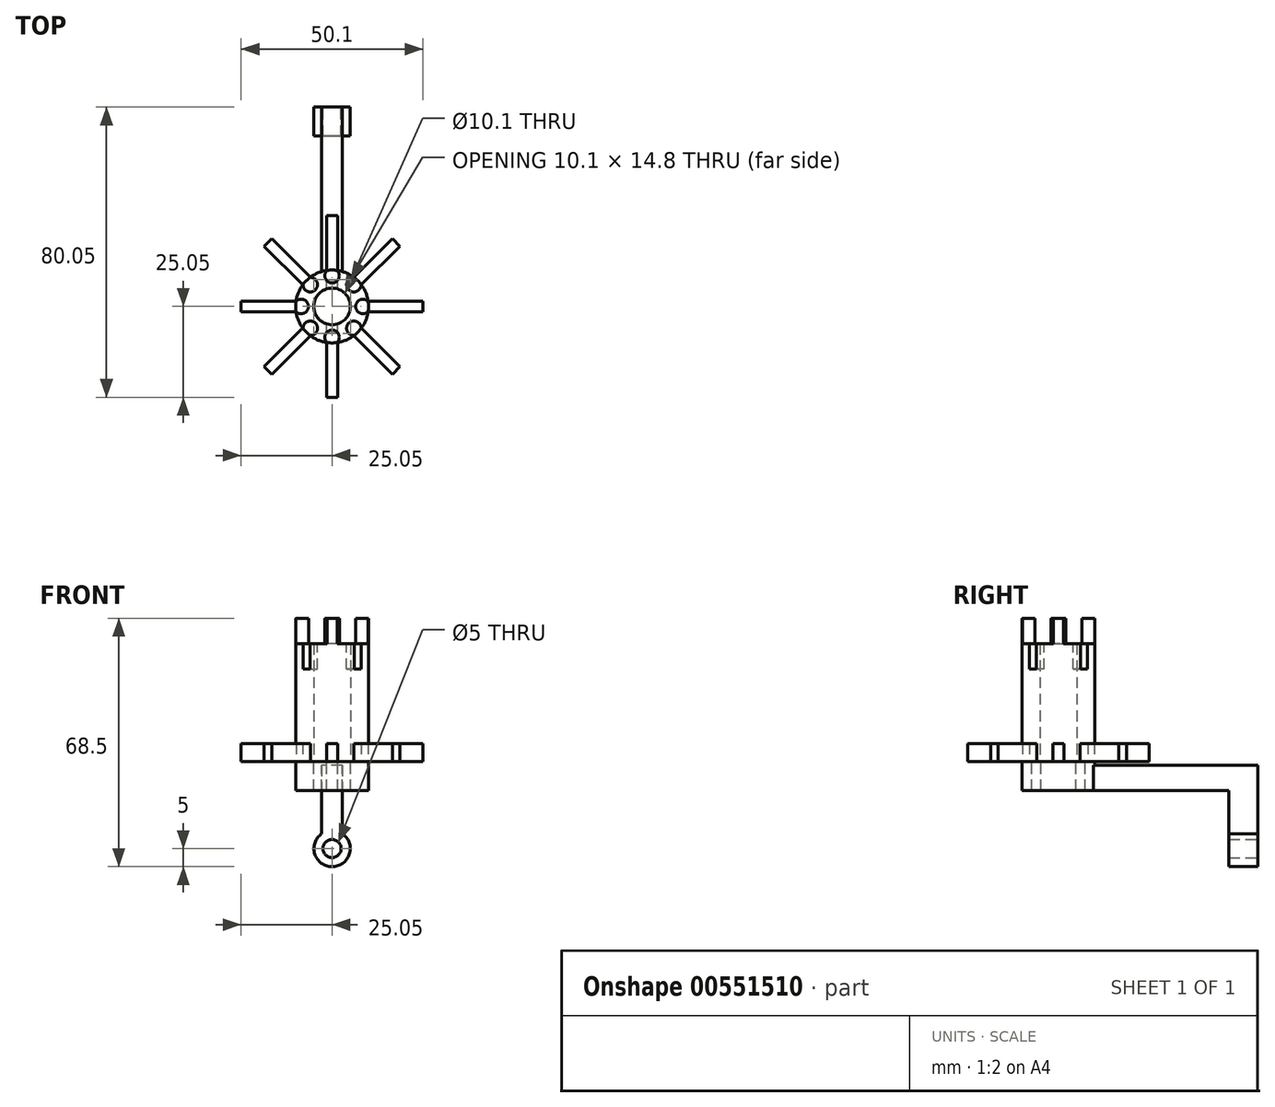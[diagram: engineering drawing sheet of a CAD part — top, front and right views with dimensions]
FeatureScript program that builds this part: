
annotation { "Feature Type Name" : "Feature", "Feature Type Description" : "" }
export const myFeature = defineFeature(function(context is Context, id is Id, definition is map)
    precondition{}
    {
        {
            var Q0;
            Q0=qCreatedBy(makeId("Front.planeOp"),FACE);
            var sketch = newSketch(context, id + "F0", { "sketchPlane" : qUnion([Q0])});
            skLineSegment(sketch, "E0.bottom", {"start": v(2.83, -1) * mm, "end": v(-2.83, -1) * mm});
            skLineSegment(sketch, "E0.top", {"start": v(2.83, -8) * mm, "end": v(-2.83, -8) * mm});
            skLineSegment(sketch, "E0.left", {"start": v(2.83, -1) * mm, "end": v(2.83, -8) * mm});
            skLineSegment(sketch, "E0.right", {"start": v(-2.83, -1) * mm, "end": v(-2.83, -8) * mm});
            skSolve(sketch);
        }
        {
            var Q0;
            Q0=qCreatedBy(makeId("Top.planeOp"),FACE);
            var sketch = newSketch(context, id + "F1", { "sketchPlane" : qUnion([Q0])});
            skCircle(sketch, "E1", {"center": v(0, 0) * mm, "radius": 5.05 * mm});
            skCircle(sketch, "E2", {"center": v(0, 0) * mm, "radius": 10.05 * mm});
            skLineSegment(sketch, "E3.bottom", {"start": v(1.5, -25.05) * mm, "end": v(-1.5, -25.05) * mm});
            skLineSegment(sketch, "E3.top", {"start": v(1.5, 25.05) * mm, "end": v(-1.5, 25.05) * mm});
            skLineSegment(sketch, "E3.left", {"start": v(1.5, -25.05) * mm, "end": v(1.5, 25.05) * mm});
            skLineSegment(sketch, "E3.right", {"start": v(-1.5, -25.05) * mm, "end": v(-1.5, 25.05) * mm});
            skLineSegment(sketch, "E4.bottom", {"start": v(25.05, -1.5) * mm, "end": v(-25.05, -1.5) * mm});
            skLineSegment(sketch, "E4.top", {"start": v(25.05, 1.5) * mm, "end": v(-25.05, 1.5) * mm});
            skLineSegment(sketch, "E4.left", {"start": v(25.05, -1.5) * mm, "end": v(25.05, 1.5) * mm});
            skLineSegment(sketch, "E4.right", {"start": v(-25.05, -1.5) * mm, "end": v(-25.05, 1.5) * mm});
            skLineSegment(sketch, "E5", {"start": v(18.74, -16.62) * mm, "end": v(-16.62, 18.74) * mm});
            skLineSegment(sketch, "E6", {"start": v(16.62, -18.74) * mm, "end": v(-18.74, 16.62) * mm});
            skLineSegment(sketch, "E7", {"start": v(-18.74, 16.62) * mm, "end": v(-16.62, 18.74) * mm});
            skLineSegment(sketch, "E8", {"start": v(16.62, -18.74) * mm, "end": v(18.74, -16.62) * mm});
            skLineSegment(sketch, "E9", {"start": v(-18.74, -16.62) * mm, "end": v(16.62, 18.74) * mm});
            skLineSegment(sketch, "E10", {"start": v(18.74, 16.62) * mm, "end": v(-16.62, -18.74) * mm});
            skLineSegment(sketch, "E11", {"start": v(-18.74, -16.62) * mm, "end": v(-16.62, -18.74) * mm});
            skLineSegment(sketch, "E12", {"start": v(16.62, 18.74) * mm, "end": v(18.74, 16.62) * mm});
            skLineSegment(sketch, "E13", {"start": v(1.5, -7.4) * mm, "end": v(-1.5, -7.4) * mm});
            skLineSegment(sketch, "E14", {"start": v(-1.5, 7.4) * mm, "end": v(1.5, 7.4) * mm});
            skSolve(sketch);
        }
        {
            var Q0;
            {var subQ0=sQuery(id+"F1.wireOp",EDGE,"E5");var subQ1=sQuery(id+"F1.wireOp",EDGE,"E1");var subQ2=makeQuery(id+"F1.imprint","INTERSECT",VERTEX,{"disambiguationData":[OD(1.0)],"derivedFrom":[subQ1,subQ0]});Q0=makeQuery(id+"F1.imprint","IMPRINT",FACE,{"disambiguationData":[TD([[makeQuery(id+"F1.imprint","IMPRINT",EDGE,{"disambiguationData":[TD([[subQ2,-1.0]])],"derivedFrom":subQ1}),-1.0]])]});}
            var Q1;
            {var subQ0=sQuery(id+"F1.wireOp",EDGE,"E6");var subQ1=sQuery(id+"F1.wireOp",EDGE,"E1");var subQ2=makeQuery(id+"F1.imprint","INTERSECT",VERTEX,{"disambiguationData":[OD(1.0)],"derivedFrom":[subQ1,subQ0]});Q1=makeQuery(id+"F1.imprint","IMPRINT",FACE,{"disambiguationData":[TD([[makeQuery(id+"F1.imprint","IMPRINT",EDGE,{"disambiguationData":[TD([[subQ2,-1.0]])],"derivedFrom":subQ1}),-1.0]])]});}
            var Q2;
            {var subQ0=sQuery(id+"F1.wireOp",EDGE,"E3.left");var subQ1=sQuery(id+"F1.wireOp",EDGE,"E1");var subQ2=makeQuery(id+"F1.imprint","INTERSECT",VERTEX,{"disambiguationData":[OD(1.0)],"derivedFrom":[subQ1,subQ0]});Q2=makeQuery(id+"F1.imprint","IMPRINT",FACE,{"disambiguationData":[TD([[makeQuery(id+"F1.imprint","IMPRINT",EDGE,{"disambiguationData":[TD([[subQ2,-1.0]])],"derivedFrom":subQ1}),-1.0]])]});}
            var Q3;
            {var subQ0=sQuery(id+"F1.wireOp",EDGE,"E3.right");var subQ1=sQuery(id+"F1.wireOp",EDGE,"E1");var subQ2=makeQuery(id+"F1.imprint","INTERSECT",VERTEX,{"disambiguationData":[OD(1.0)],"derivedFrom":[subQ1,subQ0]});Q3=makeQuery(id+"F1.imprint","IMPRINT",FACE,{"disambiguationData":[TD([[makeQuery(id+"F1.imprint","IMPRINT",EDGE,{"disambiguationData":[TD([[subQ2,-1.0]])],"derivedFrom":subQ1}),-1.0]])]});}
            var Q4;
            {var subQ0=sQuery(id+"F1.wireOp",EDGE,"E10");var subQ1=sQuery(id+"F1.wireOp",EDGE,"E1");var subQ2=makeQuery(id+"F1.imprint","INTERSECT",VERTEX,{"disambiguationData":[OD(1.0)],"derivedFrom":[subQ1,subQ0]});Q4=makeQuery(id+"F1.imprint","IMPRINT",FACE,{"disambiguationData":[TD([[makeQuery(id+"F1.imprint","IMPRINT",EDGE,{"disambiguationData":[TD([[subQ2,-1.0]])],"derivedFrom":subQ1}),-1.0]])]});}
            var Q5;
            {var subQ0=sQuery(id+"F1.wireOp",EDGE,"E9");var subQ1=sQuery(id+"F1.wireOp",EDGE,"E1");var subQ2=makeQuery(id+"F1.imprint","INTERSECT",VERTEX,{"disambiguationData":[OD(1.0)],"derivedFrom":[subQ1,subQ0]});Q5=makeQuery(id+"F1.imprint","IMPRINT",FACE,{"disambiguationData":[TD([[makeQuery(id+"F1.imprint","IMPRINT",EDGE,{"disambiguationData":[TD([[subQ2,-1.0]])],"derivedFrom":subQ1}),-1.0]])]});}
            var Q6;
            {var subQ0=sQuery(id+"F1.wireOp",EDGE,"E4.bottom");var subQ1=sQuery(id+"F1.wireOp",EDGE,"E1");var subQ2=makeQuery(id+"F1.imprint","INTERSECT",VERTEX,{"disambiguationData":[OD(0.0)],"derivedFrom":[subQ1,subQ0]});Q6=makeQuery(id+"F1.imprint","IMPRINT",FACE,{"disambiguationData":[TD([[makeQuery(id+"F1.imprint","IMPRINT",EDGE,{"disambiguationData":[TD([[subQ2,-1.0]])],"derivedFrom":subQ1}),-1.0]])]});}
            var Q7;
            {var subQ0=sQuery(id+"F1.wireOp",EDGE,"E4.top");var subQ1=sQuery(id+"F1.wireOp",EDGE,"E1");var subQ2=makeQuery(id+"F1.imprint","INTERSECT",VERTEX,{"disambiguationData":[OD(1.0)],"derivedFrom":[subQ1,subQ0]});Q7=makeQuery(id+"F1.imprint","IMPRINT",FACE,{"disambiguationData":[TD([[makeQuery(id+"F1.imprint","IMPRINT",EDGE,{"disambiguationData":[TD([[subQ2,-1.0]])],"derivedFrom":subQ1}),-1.0]])]});}
            var Q8;
            {var subQ0=sQuery(id+"F1.wireOp",EDGE,"E6");var subQ1=sQuery(id+"F1.wireOp",EDGE,"E1");var subQ2=makeQuery(id+"F1.imprint","INTERSECT",VERTEX,{"disambiguationData":[OD(0.0)],"derivedFrom":[subQ1,subQ0]});Q8=makeQuery(id+"F1.imprint","IMPRINT",FACE,{"disambiguationData":[TD([[makeQuery(id+"F1.imprint","IMPRINT",EDGE,{"disambiguationData":[TD([[subQ2,-1.0]])],"derivedFrom":subQ1}),-1.0]])]});}
            var Q9;
            {var subQ0=sQuery(id+"F1.wireOp",EDGE,"E5");var subQ1=sQuery(id+"F1.wireOp",EDGE,"E1");var subQ2=makeQuery(id+"F1.imprint","INTERSECT",VERTEX,{"disambiguationData":[OD(0.0)],"derivedFrom":[subQ1,subQ0]});Q9=makeQuery(id+"F1.imprint","IMPRINT",FACE,{"disambiguationData":[TD([[makeQuery(id+"F1.imprint","IMPRINT",EDGE,{"disambiguationData":[TD([[subQ2,-1.0]])],"derivedFrom":subQ1}),-1.0]])]});}
            var Q10;
            {var subQ0=sQuery(id+"F1.wireOp",EDGE,"E3.right");var subQ1=sQuery(id+"F1.wireOp",EDGE,"E1");var subQ2=makeQuery(id+"F1.imprint","INTERSECT",VERTEX,{"disambiguationData":[OD(0.0)],"derivedFrom":[subQ1,subQ0]});Q10=makeQuery(id+"F1.imprint","IMPRINT",FACE,{"disambiguationData":[TD([[makeQuery(id+"F1.imprint","IMPRINT",EDGE,{"disambiguationData":[TD([[subQ2,-1.0]])],"derivedFrom":subQ1}),-1.0]])]});}
            var Q11;
            {var subQ0=sQuery(id+"F1.wireOp",EDGE,"E3.left");var subQ1=sQuery(id+"F1.wireOp",EDGE,"E1");var subQ2=makeQuery(id+"F1.imprint","INTERSECT",VERTEX,{"disambiguationData":[OD(0.0)],"derivedFrom":[subQ1,subQ0]});Q11=makeQuery(id+"F1.imprint","IMPRINT",FACE,{"disambiguationData":[TD([[makeQuery(id+"F1.imprint","IMPRINT",EDGE,{"disambiguationData":[TD([[subQ2,-1.0]])],"derivedFrom":subQ1}),-1.0]])]});}
            var Q12;
            {var subQ0=sQuery(id+"F1.wireOp",EDGE,"E9");var subQ1=sQuery(id+"F1.wireOp",EDGE,"E1");var subQ2=makeQuery(id+"F1.imprint","INTERSECT",VERTEX,{"disambiguationData":[OD(0.0)],"derivedFrom":[subQ1,subQ0]});Q12=makeQuery(id+"F1.imprint","IMPRINT",FACE,{"disambiguationData":[TD([[makeQuery(id+"F1.imprint","IMPRINT",EDGE,{"disambiguationData":[TD([[subQ2,-1.0]])],"derivedFrom":subQ1}),-1.0]])]});}
            var Q13;
            {var subQ0=sQuery(id+"F1.wireOp",EDGE,"E10");var subQ1=sQuery(id+"F1.wireOp",EDGE,"E1");var subQ2=makeQuery(id+"F1.imprint","INTERSECT",VERTEX,{"disambiguationData":[OD(0.0)],"derivedFrom":[subQ1,subQ0]});Q13=makeQuery(id+"F1.imprint","IMPRINT",FACE,{"disambiguationData":[TD([[makeQuery(id+"F1.imprint","IMPRINT",EDGE,{"disambiguationData":[TD([[subQ2,-1.0]])],"derivedFrom":subQ1}),-1.0]])]});}
            var Q14;
            {var subQ0=sQuery(id+"F1.wireOp",EDGE,"E10");var subQ1=sQuery(id+"F1.wireOp",EDGE,"E1");var subQ2=makeQuery(id+"F1.imprint","INTERSECT",VERTEX,{"disambiguationData":[OD(0.0)],"derivedFrom":[subQ1,subQ0]});Q14=makeQuery(id+"F1.imprint","IMPRINT",FACE,{"disambiguationData":[TD([[makeQuery(id+"F1.imprint","IMPRINT",EDGE,{"disambiguationData":[TD([[subQ2,1.0]])],"derivedFrom":subQ1}),-1.0]])]});}
            var Q15;
            {var subQ0=sQuery(id+"F1.wireOp",EDGE,"E4.top");var subQ1=sQuery(id+"F1.wireOp",EDGE,"E1");var subQ2=makeQuery(id+"F1.imprint","INTERSECT",VERTEX,{"disambiguationData":[OD(0.0)],"derivedFrom":[subQ1,subQ0]});Q15=makeQuery(id+"F1.imprint","IMPRINT",FACE,{"disambiguationData":[TD([[makeQuery(id+"F1.imprint","IMPRINT",EDGE,{"disambiguationData":[TD([[subQ2,1.0]])],"derivedFrom":subQ1}),-1.0]])]});}
            var Q16;
            {var subQ5=sQuery(id+"F1.wireOp",EDGE,"E13");Q16=makeQuery(id+"F1.imprint","IMPRINT",FACE,{"disambiguationData":[TD([[makeQuery(id+"F1.imprint","IMPRINT",EDGE,{"derivedFrom":subQ5}),1.0]])]});}
            var Q17;
            {var subQ5=sQuery(id+"F1.wireOp",EDGE,"E14");Q17=makeQuery(id+"F1.imprint","IMPRINT",FACE,{"disambiguationData":[TD([[makeQuery(id+"F1.imprint","IMPRINT",EDGE,{"derivedFrom":subQ5}),1.0]])]});}
            extrude(context, id + "F2", {"entities" : qUnion([Q0, Q1, Q2, Q3, Q4, Q5, Q6, Q7, Q8, Q9, Q10, Q11, Q12, Q13, Q14, Q15, Q16, Q17]), "depth" : 32.5 * mm, "offsetDistance" : 25 * mm});
        }
        {
            var Q0;
            {var subQ5=sQuery(id+"F1.wireOp",EDGE,"E4.right");Q0=makeQuery(id+"F1.imprint","IMPRINT",FACE,{"disambiguationData":[TD([[makeQuery(id+"F1.imprint","IMPRINT",EDGE,{"derivedFrom":subQ5}),-1.0]])]});}
            var Q1;
            {var subQ5=sQuery(id+"F1.wireOp",EDGE,"E11");Q1=makeQuery(id+"F1.imprint","IMPRINT",FACE,{"disambiguationData":[TD([[makeQuery(id+"F1.imprint","IMPRINT",EDGE,{"derivedFrom":subQ5}),1.0]])]});}
            var Q2;
            {var subQ5=sQuery(id+"F1.wireOp",EDGE,"E3.bottom");Q2=makeQuery(id+"F1.imprint","IMPRINT",FACE,{"disambiguationData":[TD([[makeQuery(id+"F1.imprint","IMPRINT",EDGE,{"derivedFrom":subQ5}),-1.0]])]});}
            var Q3;
            {var subQ5=sQuery(id+"F1.wireOp",EDGE,"E8");Q3=makeQuery(id+"F1.imprint","IMPRINT",FACE,{"disambiguationData":[TD([[makeQuery(id+"F1.imprint","IMPRINT",EDGE,{"derivedFrom":subQ5}),1.0]])]});}
            var Q4;
            {var subQ5=sQuery(id+"F1.wireOp",EDGE,"E4.left");Q4=makeQuery(id+"F1.imprint","IMPRINT",FACE,{"disambiguationData":[TD([[makeQuery(id+"F1.imprint","IMPRINT",EDGE,{"derivedFrom":subQ5}),1.0]])]});}
            var Q5;
            {var subQ5=sQuery(id+"F1.wireOp",EDGE,"E12");Q5=makeQuery(id+"F1.imprint","IMPRINT",FACE,{"disambiguationData":[TD([[makeQuery(id+"F1.imprint","IMPRINT",EDGE,{"derivedFrom":subQ5}),-1.0]])]});}
            var Q6;
            {var subQ5=sQuery(id+"F1.wireOp",EDGE,"E3.top");Q6=makeQuery(id+"F1.imprint","IMPRINT",FACE,{"disambiguationData":[TD([[makeQuery(id+"F1.imprint","IMPRINT",EDGE,{"derivedFrom":subQ5}),1.0]])]});}
            var Q7;
            {var subQ5=sQuery(id+"F1.wireOp",EDGE,"E7");Q7=makeQuery(id+"F1.imprint","IMPRINT",FACE,{"disambiguationData":[TD([[makeQuery(id+"F1.imprint","IMPRINT",EDGE,{"derivedFrom":subQ5}),-1.0]])]});}
            extrude(context, id + "F3", {"entities" : qUnion([Q0, Q1, Q2, Q3, Q4, Q5, Q6, Q7]), "operationType" : NewBodyOperationType.ADD, "depth" : 5 * mm, "offsetDistance" : 25 * mm});
        }
        {
            var Q0;
            Q0=makeQuery(id+"F2.opExtrude","CAP_FACE",FACE,{"disambiguationData":[OSD([sQuery(id+"F1.wireOp",EDGE,"E1"),sQuery(id+"F1.wireOp",EDGE,"E2")])],"isStart":false});
            var sketch = newSketch(context, id + "F4", { "sketchPlane" : qUnion([Q0])});
            skLineSegment(sketch, "E15", {"start": v(0, 0) * mm, "end": v(8.5, 0) * mm});
            skLineSegment(sketch, "E16", {"start": v(0, 0) * mm, "end": v(0, -8.5) * mm});
            skLineSegment(sketch, "E17", {"start": v(0, 0) * mm, "end": v(-8.5, 0) * mm});
            skLineSegment(sketch, "E18", {"start": v(0, 0) * mm, "end": v(0, 8.5) * mm});
            skLineSegment(sketch, "E19", {"start": v(0, 0) * mm, "end": v(6.01, 6.01) * mm});
            skLineSegment(sketch, "E20", {"start": v(0, 0) * mm, "end": v(-6.01, 6.01) * mm});
            skLineSegment(sketch, "E21", {"start": v(0, 0) * mm, "end": v(6.01, -6.01) * mm});
            skLineSegment(sketch, "E22", {"start": v(0, 0) * mm, "end": v(-6.01, -6.01) * mm});
            skCircle(sketch, "E23", {"center": v(-8.5, 0) * mm, "radius": 2 * mm});
            skCircle(sketch, "E24", {"center": v(-6.01, -6.01) * mm, "radius": 2 * mm});
            skCircle(sketch, "E25", {"center": v(0, -8.5) * mm, "radius": 2 * mm});
            skCircle(sketch, "E26", {"center": v(6.01, -6.01) * mm, "radius": 2 * mm});
            skCircle(sketch, "E27", {"center": v(8.5, 0) * mm, "radius": 2 * mm});
            skCircle(sketch, "E28", {"center": v(6.01, 6.01) * mm, "radius": 2 * mm});
            skCircle(sketch, "E29", {"center": v(0, 8.5) * mm, "radius": 2 * mm});
            skCircle(sketch, "E30", {"center": v(-6.01, 6.01) * mm, "radius": 2 * mm});
            skSolve(sketch);
        }
        {
            var Q0;
            Q0=makeQuery(id+"F4.imprint","IMPRINT",FACE,{"disambiguationData":[TD([[makeQuery(id+"F4.imprint","IMPRINT",EDGE,{"derivedFrom":sQuery(id+"F4.wireOp",EDGE,"E25")}),1.0]])]});
            var Q1;
            Q1=makeQuery(id+"F4.imprint","IMPRINT",FACE,{"disambiguationData":[TD([[makeQuery(id+"F4.imprint","IMPRINT",EDGE,{"derivedFrom":sQuery(id+"F4.wireOp",EDGE,"E29")}),1.0]])]});
            var Q2;
            Q2=makeQuery(id+"F4.imprint","IMPRINT",FACE,{"disambiguationData":[TD([[makeQuery(id+"F4.imprint","IMPRINT",EDGE,{"derivedFrom":sQuery(id+"F4.wireOp",EDGE,"E23")}),1.0]])]});
            var Q3;
            Q3=makeQuery(id+"F4.imprint","IMPRINT",FACE,{"disambiguationData":[TD([[makeQuery(id+"F4.imprint","IMPRINT",EDGE,{"derivedFrom":sQuery(id+"F4.wireOp",EDGE,"E27")}),1.0]])]});
            extrude(context, id + "F5", {"entities" : qUnion([Q0, Q1, Q2, Q3]), "operationType" : NewBodyOperationType.ADD, "depth" : 7 * mm, "offsetDistance" : 25 * mm});
        }
        {
            var Q0;
            Q0=makeQuery(id+"F4.imprint","IMPRINT",FACE,{"disambiguationData":[TD([[makeQuery(id+"F4.imprint","IMPRINT",EDGE,{"derivedFrom":sQuery(id+"F4.wireOp",EDGE,"E24")}),1.0]])]});
            var Q1;
            Q1=makeQuery(id+"F4.imprint","IMPRINT",FACE,{"disambiguationData":[TD([[makeQuery(id+"F4.imprint","IMPRINT",EDGE,{"derivedFrom":sQuery(id+"F4.wireOp",EDGE,"E26")}),1.0]])]});
            var Q2;
            Q2=makeQuery(id+"F4.imprint","IMPRINT",FACE,{"disambiguationData":[TD([[makeQuery(id+"F4.imprint","IMPRINT",EDGE,{"derivedFrom":sQuery(id+"F4.wireOp",EDGE,"E28")}),1.0]])]});
            var Q3;
            Q3=makeQuery(id+"F4.imprint","IMPRINT",FACE,{"disambiguationData":[TD([[makeQuery(id+"F4.imprint","IMPRINT",EDGE,{"derivedFrom":sQuery(id+"F4.wireOp",EDGE,"E30")}),1.0]])]});
            extrude(context, id + "F6", {"entities" : qUnion([Q0, Q1, Q2, Q3]), "operationType" : NewBodyOperationType.REMOVE, "oppositeDirection" : true, "depth" : 7 * mm, "offsetDistance" : 25 * mm});
        }
        {
            var Q0;
            {var subQ0=sQuery(id+"F1.wireOp",EDGE,"E4.bottom");var subQ1=sQuery(id+"F1.wireOp",EDGE,"E1");var subQ2=makeQuery(id+"F1.imprint","INTERSECT",VERTEX,{"disambiguationData":[OD(0.0)],"derivedFrom":[subQ1,subQ0]});Q0=makeQuery(id+"F1.imprint","IMPRINT",FACE,{"disambiguationData":[TD([[makeQuery(id+"F1.imprint","IMPRINT",EDGE,{"disambiguationData":[TD([[subQ2,-1.0]])],"derivedFrom":subQ1}),-1.0]])]});}
            var Q1;
            {var subQ0=sQuery(id+"F1.wireOp",EDGE,"E9");var subQ1=sQuery(id+"F1.wireOp",EDGE,"E1");var subQ2=makeQuery(id+"F1.imprint","INTERSECT",VERTEX,{"disambiguationData":[OD(1.0)],"derivedFrom":[subQ1,subQ0]});Q1=makeQuery(id+"F1.imprint","IMPRINT",FACE,{"disambiguationData":[TD([[makeQuery(id+"F1.imprint","IMPRINT",EDGE,{"disambiguationData":[TD([[subQ2,-1.0]])],"derivedFrom":subQ1}),-1.0]])]});}
            var Q2;
            {var subQ0=sQuery(id+"F1.wireOp",EDGE,"E10");var subQ1=sQuery(id+"F1.wireOp",EDGE,"E1");var subQ2=makeQuery(id+"F1.imprint","INTERSECT",VERTEX,{"disambiguationData":[OD(1.0)],"derivedFrom":[subQ1,subQ0]});Q2=makeQuery(id+"F1.imprint","IMPRINT",FACE,{"disambiguationData":[TD([[makeQuery(id+"F1.imprint","IMPRINT",EDGE,{"disambiguationData":[TD([[subQ2,-1.0]])],"derivedFrom":subQ1}),-1.0]])]});}
            var Q3;
            {var subQ0=sQuery(id+"F1.wireOp",EDGE,"E3.left");var subQ1=sQuery(id+"F1.wireOp",EDGE,"E1");var subQ2=makeQuery(id+"F1.imprint","INTERSECT",VERTEX,{"disambiguationData":[OD(1.0)],"derivedFrom":[subQ1,subQ0]});Q3=makeQuery(id+"F1.imprint","IMPRINT",FACE,{"disambiguationData":[TD([[makeQuery(id+"F1.imprint","IMPRINT",EDGE,{"disambiguationData":[TD([[subQ2,-1.0]])],"derivedFrom":subQ1}),-1.0]])]});}
            var Q4;
            {var subQ0=sQuery(id+"F1.wireOp",EDGE,"E6");var subQ1=sQuery(id+"F1.wireOp",EDGE,"E1");var subQ2=makeQuery(id+"F1.imprint","INTERSECT",VERTEX,{"disambiguationData":[OD(1.0)],"derivedFrom":[subQ1,subQ0]});Q4=makeQuery(id+"F1.imprint","IMPRINT",FACE,{"disambiguationData":[TD([[makeQuery(id+"F1.imprint","IMPRINT",EDGE,{"disambiguationData":[TD([[subQ2,-1.0]])],"derivedFrom":subQ1}),-1.0]])]});}
            var Q5;
            {var subQ0=sQuery(id+"F1.wireOp",EDGE,"E5");var subQ1=sQuery(id+"F1.wireOp",EDGE,"E1");var subQ2=makeQuery(id+"F1.imprint","INTERSECT",VERTEX,{"disambiguationData":[OD(1.0)],"derivedFrom":[subQ1,subQ0]});Q5=makeQuery(id+"F1.imprint","IMPRINT",FACE,{"disambiguationData":[TD([[makeQuery(id+"F1.imprint","IMPRINT",EDGE,{"disambiguationData":[TD([[subQ2,-1.0]])],"derivedFrom":subQ1}),-1.0]])]});}
            var Q6;
            {var subQ0=sQuery(id+"F1.wireOp",EDGE,"E4.top");var subQ1=sQuery(id+"F1.wireOp",EDGE,"E1");var subQ2=makeQuery(id+"F1.imprint","INTERSECT",VERTEX,{"disambiguationData":[OD(0.0)],"derivedFrom":[subQ1,subQ0]});Q6=makeQuery(id+"F1.imprint","IMPRINT",FACE,{"disambiguationData":[TD([[makeQuery(id+"F1.imprint","IMPRINT",EDGE,{"disambiguationData":[TD([[subQ2,1.0]])],"derivedFrom":subQ1}),-1.0]])]});}
            var Q7;
            {var subQ0=sQuery(id+"F1.wireOp",EDGE,"E10");var subQ1=sQuery(id+"F1.wireOp",EDGE,"E1");var subQ2=makeQuery(id+"F1.imprint","INTERSECT",VERTEX,{"disambiguationData":[OD(0.0)],"derivedFrom":[subQ1,subQ0]});Q7=makeQuery(id+"F1.imprint","IMPRINT",FACE,{"disambiguationData":[TD([[makeQuery(id+"F1.imprint","IMPRINT",EDGE,{"disambiguationData":[TD([[subQ2,1.0]])],"derivedFrom":subQ1}),-1.0]])]});}
            var Q8;
            {var subQ0=sQuery(id+"F1.wireOp",EDGE,"E10");var subQ1=sQuery(id+"F1.wireOp",EDGE,"E1");var subQ2=makeQuery(id+"F1.imprint","INTERSECT",VERTEX,{"disambiguationData":[OD(0.0)],"derivedFrom":[subQ1,subQ0]});Q8=makeQuery(id+"F1.imprint","IMPRINT",FACE,{"disambiguationData":[TD([[makeQuery(id+"F1.imprint","IMPRINT",EDGE,{"disambiguationData":[TD([[subQ2,-1.0]])],"derivedFrom":subQ1}),-1.0]])]});}
            var Q9;
            {var subQ0=sQuery(id+"F1.wireOp",EDGE,"E9");var subQ1=sQuery(id+"F1.wireOp",EDGE,"E1");var subQ2=makeQuery(id+"F1.imprint","INTERSECT",VERTEX,{"disambiguationData":[OD(0.0)],"derivedFrom":[subQ1,subQ0]});Q9=makeQuery(id+"F1.imprint","IMPRINT",FACE,{"disambiguationData":[TD([[makeQuery(id+"F1.imprint","IMPRINT",EDGE,{"disambiguationData":[TD([[subQ2,-1.0]])],"derivedFrom":subQ1}),-1.0]])]});}
            var Q10;
            {var subQ0=sQuery(id+"F1.wireOp",EDGE,"E3.right");var subQ1=sQuery(id+"F1.wireOp",EDGE,"E1");var subQ2=makeQuery(id+"F1.imprint","INTERSECT",VERTEX,{"disambiguationData":[OD(0.0)],"derivedFrom":[subQ1,subQ0]});Q10=makeQuery(id+"F1.imprint","IMPRINT",FACE,{"disambiguationData":[TD([[makeQuery(id+"F1.imprint","IMPRINT",EDGE,{"disambiguationData":[TD([[subQ2,-1.0]])],"derivedFrom":subQ1}),-1.0]])]});}
            var Q11;
            {var subQ0=sQuery(id+"F1.wireOp",EDGE,"E5");var subQ1=sQuery(id+"F1.wireOp",EDGE,"E1");var subQ2=makeQuery(id+"F1.imprint","INTERSECT",VERTEX,{"disambiguationData":[OD(0.0)],"derivedFrom":[subQ1,subQ0]});Q11=makeQuery(id+"F1.imprint","IMPRINT",FACE,{"disambiguationData":[TD([[makeQuery(id+"F1.imprint","IMPRINT",EDGE,{"disambiguationData":[TD([[subQ2,-1.0]])],"derivedFrom":subQ1}),-1.0]])]});}
            var Q12;
            {var subQ0=sQuery(id+"F1.wireOp",EDGE,"E6");var subQ1=sQuery(id+"F1.wireOp",EDGE,"E1");var subQ2=makeQuery(id+"F1.imprint","INTERSECT",VERTEX,{"disambiguationData":[OD(0.0)],"derivedFrom":[subQ1,subQ0]});Q12=makeQuery(id+"F1.imprint","IMPRINT",FACE,{"disambiguationData":[TD([[makeQuery(id+"F1.imprint","IMPRINT",EDGE,{"disambiguationData":[TD([[subQ2,-1.0]])],"derivedFrom":subQ1}),-1.0]])]});}
            var Q13;
            {var subQ0=sQuery(id+"F1.wireOp",EDGE,"E4.top");var subQ1=sQuery(id+"F1.wireOp",EDGE,"E1");var subQ2=makeQuery(id+"F1.imprint","INTERSECT",VERTEX,{"disambiguationData":[OD(1.0)],"derivedFrom":[subQ1,subQ0]});Q13=makeQuery(id+"F1.imprint","IMPRINT",FACE,{"disambiguationData":[TD([[makeQuery(id+"F1.imprint","IMPRINT",EDGE,{"disambiguationData":[TD([[subQ2,-1.0]])],"derivedFrom":subQ1}),-1.0]])]});}
            var Q14;
            {var subQ5=sQuery(id+"F1.wireOp",EDGE,"E14");Q14=makeQuery(id+"F1.imprint","IMPRINT",FACE,{"disambiguationData":[TD([[makeQuery(id+"F1.imprint","IMPRINT",EDGE,{"derivedFrom":subQ5}),1.0]])]});}
            var Q15;
            {var subQ5=sQuery(id+"F1.wireOp",EDGE,"E13");Q15=makeQuery(id+"F1.imprint","IMPRINT",FACE,{"disambiguationData":[TD([[makeQuery(id+"F1.imprint","IMPRINT",EDGE,{"derivedFrom":subQ5}),1.0]])]});}
            extrude(context, id + "F7", {"entities" : qUnion([Q0, Q1, Q2, Q3, Q4, Q5, Q6, Q7, Q8, Q9, Q10, Q11, Q12, Q13, Q14, Q15]), "oppositeDirection" : true, "depth" : 8 * mm, "offsetDistance" : 25 * mm});
        }
        {
            var Q0;
            Q0=makeQuery(id+"F0.imprint","IMPRINT",FACE,{"disambiguationData":[TD([[makeQuery(id+"F0.imprint","IMPRINT",EDGE,{"derivedFrom":sQuery(id+"F0.wireOp",EDGE,"E0.bottom")}),1.0]])]});
            extrude(context, id + "F8", {"entities" : qUnion([Q0]), "operationType" : NewBodyOperationType.ADD, "oppositeDirection" : true, "depth" : 55 * mm, "offsetDistance" : 25 * mm});
        }
        {
            var Q0;
            {var subQ0=sQuery(id+"F1.wireOp",EDGE,"E5");var subQ1=sQuery(id+"F1.wireOp",EDGE,"E3.left");var subQ2=makeQuery(id+"F1.imprint","INTERSECT",VERTEX,{"derivedFrom":[subQ1,subQ0]});Q0=makeQuery(id+"F1.imprint","IMPRINT",FACE,{"disambiguationData":[TD([[makeQuery(id+"F1.imprint","IMPRINT",EDGE,{"disambiguationData":[TD([[subQ2,-1.0]])],"derivedFrom":subQ1}),-1.0]])]});}
            var Q1;
            {var subQ0=sQuery(id+"F1.wireOp",EDGE,"E9");var subQ1=sQuery(id+"F1.wireOp",EDGE,"E1");var subQ2=makeQuery(id+"F1.imprint","INTERSECT",VERTEX,{"disambiguationData":[OD(1.0)],"derivedFrom":[subQ1,subQ0]});Q1=makeQuery(id+"F1.imprint","IMPRINT",FACE,{"disambiguationData":[TD([[makeQuery(id+"F1.imprint","IMPRINT",EDGE,{"disambiguationData":[TD([[subQ2,-1.0]])],"derivedFrom":subQ1}),1.0]])]});}
            var Q2;
            {var subQ0=sQuery(id+"F1.wireOp",EDGE,"E4.top");var subQ1=sQuery(id+"F1.wireOp",EDGE,"E1");var subQ2=makeQuery(id+"F1.imprint","INTERSECT",VERTEX,{"disambiguationData":[OD(1.0)],"derivedFrom":[subQ1,subQ0]});Q2=makeQuery(id+"F1.imprint","IMPRINT",FACE,{"disambiguationData":[TD([[makeQuery(id+"F1.imprint","IMPRINT",EDGE,{"disambiguationData":[TD([[subQ2,-1.0]])],"derivedFrom":subQ1}),1.0]])]});}
            var Q3;
            {var subQ0=sQuery(id+"F1.wireOp",EDGE,"E9");var subQ1=sQuery(id+"F1.wireOp",EDGE,"E3.right");var subQ2=makeQuery(id+"F1.imprint","INTERSECT",VERTEX,{"derivedFrom":[subQ1,subQ0]});Q3=makeQuery(id+"F1.imprint","IMPRINT",FACE,{"disambiguationData":[TD([[makeQuery(id+"F1.imprint","IMPRINT",EDGE,{"disambiguationData":[TD([[subQ2,-1.0]])],"derivedFrom":subQ1}),1.0]])]});}
            var Q4;
            {var subQ5=sQuery(id+"F1.wireOp",EDGE,"E5");var subQ7=sQuery(id+"F1.wireOp",EDGE,"E1");var subQ8=makeQuery(id+"F1.imprint","INTERSECT",VERTEX,{"disambiguationData":[OD(0.0)],"derivedFrom":[subQ7,subQ5]});Q4=makeQuery(id+"F1.imprint","IMPRINT",FACE,{"disambiguationData":[TD([[makeQuery(id+"F1.imprint","IMPRINT",EDGE,{"disambiguationData":[TD([[subQ8,-1.0]])],"derivedFrom":subQ7}),1.0]])]});}
            var Q5;
            {var subQ0=sQuery(id+"F1.wireOp",EDGE,"E4.top");var subQ1=sQuery(id+"F1.wireOp",EDGE,"E3.right");var subQ2=makeQuery(id+"F1.imprint","INTERSECT",VERTEX,{"derivedFrom":[subQ1,subQ0]});Q5=makeQuery(id+"F1.imprint","IMPRINT",FACE,{"disambiguationData":[TD([[makeQuery(id+"F1.imprint","IMPRINT",EDGE,{"disambiguationData":[TD([[subQ2,-1.0]])],"derivedFrom":subQ1}),-1.0]])]});}
            var Q6;
            {var subQ5=sQuery(id+"F1.wireOp",EDGE,"E3.left");var subQ6=sQuery(id+"F1.wireOp",EDGE,"E1");var subQ7=makeQuery(id+"F1.imprint","INTERSECT",VERTEX,{"disambiguationData":[OD(0.0)],"derivedFrom":[subQ6,subQ5]});Q6=makeQuery(id+"F1.imprint","IMPRINT",FACE,{"disambiguationData":[TD([[makeQuery(id+"F1.imprint","IMPRINT",EDGE,{"disambiguationData":[TD([[subQ7,-1.0]])],"derivedFrom":subQ6}),1.0]])]});}
            var Q7;
            {var subQ0=sQuery(id+"F1.wireOp",EDGE,"E4.top");var subQ1=sQuery(id+"F1.wireOp",EDGE,"E3.left");var subQ2=makeQuery(id+"F1.imprint","INTERSECT",VERTEX,{"derivedFrom":[subQ1,subQ0]});Q7=makeQuery(id+"F1.imprint","IMPRINT",FACE,{"disambiguationData":[TD([[makeQuery(id+"F1.imprint","IMPRINT",EDGE,{"disambiguationData":[TD([[subQ2,-1.0]])],"derivedFrom":subQ1}),1.0]])]});}
            var Q8;
            {var subQ3=sQuery(id+"F1.wireOp",EDGE,"E10");var subQ6=sQuery(id+"F1.wireOp",EDGE,"E1");var subQ9=makeQuery(id+"F1.imprint","INTERSECT",VERTEX,{"disambiguationData":[OD(0.0)],"derivedFrom":[subQ6,subQ3]});Q8=makeQuery(id+"F1.imprint","IMPRINT",FACE,{"disambiguationData":[TD([[makeQuery(id+"F1.imprint","IMPRINT",EDGE,{"disambiguationData":[TD([[subQ9,-1.0]])],"derivedFrom":subQ6}),1.0]])]});}
            var Q9;
            {var subQ0=sQuery(id+"F1.wireOp",EDGE,"E9");var subQ1=sQuery(id+"F1.wireOp",EDGE,"E1");var subQ2=makeQuery(id+"F1.imprint","INTERSECT",VERTEX,{"disambiguationData":[OD(0.0)],"derivedFrom":[subQ1,subQ0]});Q9=makeQuery(id+"F1.imprint","IMPRINT",FACE,{"disambiguationData":[TD([[makeQuery(id+"F1.imprint","IMPRINT",EDGE,{"disambiguationData":[TD([[subQ2,-1.0]])],"derivedFrom":subQ1}),1.0]])]});}
            var Q10;
            {var subQ0=sQuery(id+"F1.wireOp",EDGE,"E3.right");var subQ1=sQuery(id+"F1.wireOp",EDGE,"E1");var subQ2=makeQuery(id+"F1.imprint","INTERSECT",VERTEX,{"disambiguationData":[OD(0.0)],"derivedFrom":[subQ1,subQ0]});Q10=makeQuery(id+"F1.imprint","IMPRINT",FACE,{"disambiguationData":[TD([[makeQuery(id+"F1.imprint","IMPRINT",EDGE,{"disambiguationData":[TD([[subQ2,-1.0]])],"derivedFrom":subQ1}),1.0]])]});}
            var Q11;
            {var subQ0=sQuery(id+"F1.wireOp",EDGE,"E5");var subQ1=sQuery(id+"F1.wireOp",EDGE,"E3.left");var subQ2=makeQuery(id+"F1.imprint","INTERSECT",VERTEX,{"derivedFrom":[subQ1,subQ0]});Q11=makeQuery(id+"F1.imprint","IMPRINT",FACE,{"disambiguationData":[TD([[makeQuery(id+"F1.imprint","IMPRINT",EDGE,{"disambiguationData":[TD([[subQ2,-1.0]])],"derivedFrom":subQ1}),1.0]])]});}
            var Q12;
            {var subQ0=sQuery(id+"F1.wireOp",EDGE,"E5");var subQ1=sQuery(id+"F1.wireOp",EDGE,"E4.top");var subQ2=makeQuery(id+"F1.imprint","INTERSECT",VERTEX,{"derivedFrom":[subQ1,subQ0]});Q12=makeQuery(id+"F1.imprint","IMPRINT",FACE,{"disambiguationData":[TD([[makeQuery(id+"F1.imprint","IMPRINT",EDGE,{"disambiguationData":[TD([[subQ2,-1.0]])],"derivedFrom":subQ1}),-1.0]])]});}
            var Q13;
            {var subQ0=sQuery(id+"F1.wireOp",EDGE,"E9");var subQ1=sQuery(id+"F1.wireOp",EDGE,"E3.right");var subQ2=makeQuery(id+"F1.imprint","INTERSECT",VERTEX,{"derivedFrom":[subQ1,subQ0]});Q13=makeQuery(id+"F1.imprint","IMPRINT",FACE,{"disambiguationData":[TD([[makeQuery(id+"F1.imprint","IMPRINT",EDGE,{"disambiguationData":[TD([[subQ2,-1.0]])],"derivedFrom":subQ1}),-1.0]])]});}
            var Q14;
            {var subQ5=sQuery(id+"F1.wireOp",EDGE,"E10");var subQ13=sQuery(id+"F1.wireOp",EDGE,"E3.left");var subQ14=makeQuery(id+"F1.imprint","INTERSECT",VERTEX,{"derivedFrom":[subQ13,subQ5]});Q14=makeQuery(id+"F1.imprint","IMPRINT",FACE,{"disambiguationData":[TD([[makeQuery(id+"F1.imprint","IMPRINT",EDGE,{"disambiguationData":[TD([[subQ14,-1.0]])],"derivedFrom":subQ13}),1.0]])]});}
            var Q15;
            {var subQ0=sQuery(id+"F1.wireOp",EDGE,"E4.bottom");var subQ1=sQuery(id+"F1.wireOp",EDGE,"E3.right");var subQ2=makeQuery(id+"F1.imprint","INTERSECT",VERTEX,{"derivedFrom":[subQ1,subQ0]});Q15=makeQuery(id+"F1.imprint","IMPRINT",FACE,{"disambiguationData":[TD([[makeQuery(id+"F1.imprint","IMPRINT",EDGE,{"disambiguationData":[TD([[subQ2,-1.0]])],"derivedFrom":subQ1}),-1.0]])]});}
            var Q16;
            {var subQ0=sQuery(id+"F1.wireOp",EDGE,"E4.bottom");var subQ1=sQuery(id+"F1.wireOp",EDGE,"E3.right");var subQ2=makeQuery(id+"F1.imprint","INTERSECT",VERTEX,{"derivedFrom":[subQ1,subQ0]});Q16=makeQuery(id+"F1.imprint","IMPRINT",FACE,{"disambiguationData":[TD([[makeQuery(id+"F1.imprint","IMPRINT",EDGE,{"disambiguationData":[TD([[subQ2,-1.0]])],"derivedFrom":subQ1}),1.0]])]});}
            var Q17;
            {var subQ0=sQuery(id+"F1.wireOp",EDGE,"E6");var subQ1=sQuery(id+"F1.wireOp",EDGE,"E3.right");var subQ2=makeQuery(id+"F1.imprint","INTERSECT",VERTEX,{"derivedFrom":[subQ1,subQ0]});Q17=makeQuery(id+"F1.imprint","IMPRINT",FACE,{"disambiguationData":[TD([[makeQuery(id+"F1.imprint","IMPRINT",EDGE,{"disambiguationData":[TD([[subQ2,-1.0]])],"derivedFrom":subQ1}),1.0]])]});}
            var Q18;
            {var subQ0=sQuery(id+"F1.wireOp",EDGE,"E10");var subQ1=sQuery(id+"F1.wireOp",EDGE,"E3.right");var subQ2=makeQuery(id+"F1.imprint","INTERSECT",VERTEX,{"derivedFrom":[subQ1,subQ0]});Q18=makeQuery(id+"F1.imprint","IMPRINT",FACE,{"disambiguationData":[TD([[makeQuery(id+"F1.imprint","IMPRINT",EDGE,{"disambiguationData":[TD([[subQ2,-1.0]])],"derivedFrom":subQ1}),-1.0]])]});}
            var Q19;
            {var subQ0=sQuery(id+"F1.wireOp",EDGE,"E6");var subQ1=sQuery(id+"F1.wireOp",EDGE,"E3.left");var subQ2=makeQuery(id+"F1.imprint","INTERSECT",VERTEX,{"derivedFrom":[subQ1,subQ0]});Q19=makeQuery(id+"F1.imprint","IMPRINT",FACE,{"disambiguationData":[TD([[makeQuery(id+"F1.imprint","IMPRINT",EDGE,{"disambiguationData":[TD([[subQ2,-1.0]])],"derivedFrom":subQ1}),1.0]])]});}
            var Q20;
            {var subQ0=sQuery(id+"F1.wireOp",EDGE,"E10");var subQ1=sQuery(id+"F1.wireOp",EDGE,"E4.bottom");var subQ2=makeQuery(id+"F1.imprint","INTERSECT",VERTEX,{"derivedFrom":[subQ1,subQ0]});Q20=makeQuery(id+"F1.imprint","IMPRINT",FACE,{"disambiguationData":[TD([[makeQuery(id+"F1.imprint","IMPRINT",EDGE,{"disambiguationData":[TD([[subQ2,-1.0]])],"derivedFrom":subQ1}),1.0]])]});}
            var Q21;
            {var subQ1=sQuery(id+"F1.wireOp",EDGE,"E1");var subQ5=sQuery(id+"F1.wireOp",EDGE,"E6");var subQ6=makeQuery(id+"F1.imprint","INTERSECT",VERTEX,{"disambiguationData":[OD(1.0)],"derivedFrom":[subQ1,subQ5]});Q21=makeQuery(id+"F1.imprint","IMPRINT",FACE,{"disambiguationData":[TD([[makeQuery(id+"F1.imprint","IMPRINT",EDGE,{"disambiguationData":[TD([[subQ6,-1.0]])],"derivedFrom":subQ1}),1.0]])]});}
            var Q22;
            {var subQ0=sQuery(id+"F1.wireOp",EDGE,"E4.bottom");var subQ1=sQuery(id+"F1.wireOp",EDGE,"E3.left");var subQ2=makeQuery(id+"F1.imprint","INTERSECT",VERTEX,{"derivedFrom":[subQ1,subQ0]});Q22=makeQuery(id+"F1.imprint","IMPRINT",FACE,{"disambiguationData":[TD([[makeQuery(id+"F1.imprint","IMPRINT",EDGE,{"disambiguationData":[TD([[subQ2,-1.0]])],"derivedFrom":subQ1}),-1.0]])]});}
            var Q23;
            {var subQ0=sQuery(id+"F1.wireOp",EDGE,"E4.bottom");var subQ1=sQuery(id+"F1.wireOp",EDGE,"E3.left");var subQ2=makeQuery(id+"F1.imprint","INTERSECT",VERTEX,{"derivedFrom":[subQ1,subQ0]});Q23=makeQuery(id+"F1.imprint","IMPRINT",FACE,{"disambiguationData":[TD([[makeQuery(id+"F1.imprint","IMPRINT",EDGE,{"disambiguationData":[TD([[subQ2,-1.0]])],"derivedFrom":subQ1}),1.0]])]});}
            var Q24;
            {var subQ0=sQuery(id+"F1.wireOp",EDGE,"E10");var subQ1=sQuery(id+"F1.wireOp",EDGE,"E3.left");var subQ2=makeQuery(id+"F1.imprint","INTERSECT",VERTEX,{"derivedFrom":[subQ1,subQ0]});Q24=makeQuery(id+"F1.imprint","IMPRINT",FACE,{"disambiguationData":[TD([[makeQuery(id+"F1.imprint","IMPRINT",EDGE,{"disambiguationData":[TD([[subQ2,-1.0]])],"derivedFrom":subQ1}),-1.0]])]});}
            var Q25;
            {var subQ5=sQuery(id+"F1.wireOp",EDGE,"E4.top");var subQ6=sQuery(id+"F1.wireOp",EDGE,"E1");var subQ7=makeQuery(id+"F1.imprint","INTERSECT",VERTEX,{"disambiguationData":[OD(0.0)],"derivedFrom":[subQ6,subQ5]});Q25=makeQuery(id+"F1.imprint","IMPRINT",FACE,{"disambiguationData":[TD([[makeQuery(id+"F1.imprint","IMPRINT",EDGE,{"disambiguationData":[TD([[subQ7,1.0]])],"derivedFrom":subQ6}),1.0]])]});}
            var Q26;
            {var subQ0=sQuery(id+"F1.wireOp",EDGE,"E6");var subQ1=sQuery(id+"F1.wireOp",EDGE,"E1");var subQ2=makeQuery(id+"F1.imprint","INTERSECT",VERTEX,{"disambiguationData":[OD(0.0)],"derivedFrom":[subQ1,subQ0]});Q26=makeQuery(id+"F1.imprint","IMPRINT",FACE,{"disambiguationData":[TD([[makeQuery(id+"F1.imprint","IMPRINT",EDGE,{"disambiguationData":[TD([[subQ2,-1.0]])],"derivedFrom":subQ1}),1.0]])]});}
            var Q27;
            {var subQ0=sQuery(id+"F1.wireOp",EDGE,"E10");var subQ1=sQuery(id+"F1.wireOp",EDGE,"E1");var subQ2=makeQuery(id+"F1.imprint","INTERSECT",VERTEX,{"disambiguationData":[OD(0.0)],"derivedFrom":[subQ1,subQ0]});Q27=makeQuery(id+"F1.imprint","IMPRINT",FACE,{"disambiguationData":[TD([[makeQuery(id+"F1.imprint","IMPRINT",EDGE,{"disambiguationData":[TD([[subQ2,1.0]])],"derivedFrom":subQ1}),1.0]])]});}
            var Q28;
            {var subQ0=sQuery(id+"F1.wireOp",EDGE,"E5");var subQ1=sQuery(id+"F1.wireOp",EDGE,"E1");var subQ2=makeQuery(id+"F1.imprint","INTERSECT",VERTEX,{"disambiguationData":[OD(1.0)],"derivedFrom":[subQ1,subQ0]});Q28=makeQuery(id+"F1.imprint","IMPRINT",FACE,{"disambiguationData":[TD([[makeQuery(id+"F1.imprint","IMPRINT",EDGE,{"disambiguationData":[TD([[subQ2,-1.0]])],"derivedFrom":subQ1}),1.0]])]});}
            var Q29;
            {var subQ0=sQuery(id+"F1.wireOp",EDGE,"E4.bottom");var subQ1=sQuery(id+"F1.wireOp",EDGE,"E1");var subQ2=makeQuery(id+"F1.imprint","INTERSECT",VERTEX,{"disambiguationData":[OD(0.0)],"derivedFrom":[subQ1,subQ0]});Q29=makeQuery(id+"F1.imprint","IMPRINT",FACE,{"disambiguationData":[TD([[makeQuery(id+"F1.imprint","IMPRINT",EDGE,{"disambiguationData":[TD([[subQ2,-1.0]])],"derivedFrom":subQ1}),1.0]])]});}
            extrude(context, id + "F9", {"entities" : qUnion([Q0, Q1, Q2, Q3, Q4, Q5, Q6, Q7, Q8, Q9, Q10, Q11, Q12, Q13, Q14, Q15, Q16, Q17, Q18, Q19, Q20, Q21, Q22, Q23, Q24, Q25, Q26, Q27, Q28, Q29]), "operationType" : NewBodyOperationType.REMOVE, "oppositeDirection" : true, "depth" : 25 * mm, "offsetDistance" : 25 * mm});
        }
        {
            var Q0;
            Q0=makeQuery(id+"F8.boolean.opBoolean","MERGE",FACE,{"derivedFrom":[makeQuery(id+"F7.opExtrude","CAP_FACE",FACE,{"disambiguationData":[OSD([sQuery(id+"F1.wireOp",EDGE,"E1"),sQuery(id+"F1.wireOp",EDGE,"E2")])],"isStart":false}),makeQuery(id+"F8.opExtrude","SWEPT_FACE",FACE,{"disambiguationData":[OSD([sQuery(id+"F0.wireOp",EDGE,"E0.top")])]})]});
            var sketch = newSketch(context, id + "F10", { "sketchPlane" : qUnion([Q0])});
            skLineSegment(sketch, "E31", {"start": v(-2.83, -55) * mm, "end": v(2.83, -55) * mm});
            skLineSegment(sketch, "E32", {"start": v(2.83, -55) * mm, "end": v(2.83, -47) * mm});
            skLineSegment(sketch, "E33", {"start": v(-2.83, -55) * mm, "end": v(-2.83, -47) * mm});
            skLineSegment(sketch, "E34", {"start": v(-2.83, -47) * mm, "end": v(2.83, -47) * mm});
            skSolve(sketch);
        }
        {
            var Q0;
            Q0=makeQuery(id+"F10.imprint","IMPRINT",FACE,{"disambiguationData":[TD([[makeQuery(id+"F10.imprint","IMPRINT",EDGE,{"derivedFrom":sQuery(id+"F10.wireOp",EDGE,"E31")}),-1.0]])]});
            extrude(context, id + "F11", {"entities" : qUnion([Q0]), "operationType" : NewBodyOperationType.ADD, "depth" : 20 * mm, "offsetDistance" : 25 * mm});
        }
        {
            var Q0;
            {var subQ5=sQuery(id+"F1.wireOp",EDGE,"E14");Q0=makeQuery(id+"F1.imprint","IMPRINT",FACE,{"disambiguationData":[TD([[makeQuery(id+"F1.imprint","IMPRINT",EDGE,{"derivedFrom":subQ5}),-1.0]])]});}
            extrude(context, id + "F12", {"entities" : qUnion([Q0]), "operationType" : NewBodyOperationType.REMOVE, "oppositeDirection" : true, "depth" : 8 * mm, "offsetDistance" : 25 * mm});
        }
        {
            var Q0;
            Q0=makeQuery(id+"F11.boolean.opBoolean","MERGE",FACE,{"derivedFrom":[makeQuery(id+"F8.opExtrude","CAP_FACE",FACE,{"disambiguationData":[OSD([sQuery(id+"F0.wireOp",EDGE,"E0.bottom"),sQuery(id+"F0.wireOp",EDGE,"E0.top"),sQuery(id+"F0.wireOp",EDGE,"E0.left"),sQuery(id+"F0.wireOp",EDGE,"E0.right")])],"isStart":false}),makeQuery(id+"F11.opExtrude","SWEPT_FACE",FACE,{"disambiguationData":[OSD([sQuery(id+"F10.wireOp",EDGE,"E31")])]})]});
            var sketch = newSketch(context, id + "F13", { "sketchPlane" : qUnion([Q0])});
            skLineSegment(sketch, "E35", {"start": v(0, -1) * mm, "end": v(0, -24) * mm});
            skPoint(sketch, "E35.endSnap0", {"position": v(0, -1) * mm});
            skCircle(sketch, "E36", {"center": v(0, -24) * mm, "radius": 2.5 * mm});
            skCircle(sketch, "E37", {"center": v(0, -24) * mm, "radius": 5 * mm});
            skSolve(sketch);
        }
        {
            var Q0;
            {var subQ1=sQuery(id+"F10.wireOp",EDGE,"E31");var subQ6=makeQuery(id+"F11.opExtrude","CAP_EDGE",EDGE,{"disambiguationData":[OSD([subQ1])],"isStart":false});Q0=makeQuery(id+"F13.imprint","IMPRINT",FACE,{"disambiguationData":[TD([[makeQuery(id+"F13.imprint","IMPRINT",EDGE,{"derivedFrom":subQ6}),-1.0]])]});}
            extrude(context, id + "F14", {"entities" : qUnion([Q0]), "operationType" : NewBodyOperationType.ADD, "oppositeDirection" : true, "depth" : 8 * mm, "offsetDistance" : 25 * mm});
        }
        {
            var Q0;
            Q0=makeQuery(id+"F13.imprint","IMPRINT",FACE,{"disambiguationData":[TD([[makeQuery(id+"F13.imprint","IMPRINT",EDGE,{"derivedFrom":sQuery(id+"F13.wireOp",EDGE,"E36")}),1.0]])]});
            extrude(context, id + "F15", {"entities" : qUnion([Q0]), "operationType" : NewBodyOperationType.REMOVE, "oppositeDirection" : true, "depth" : 8 * mm, "offsetDistance" : 25 * mm});
        }
    });
